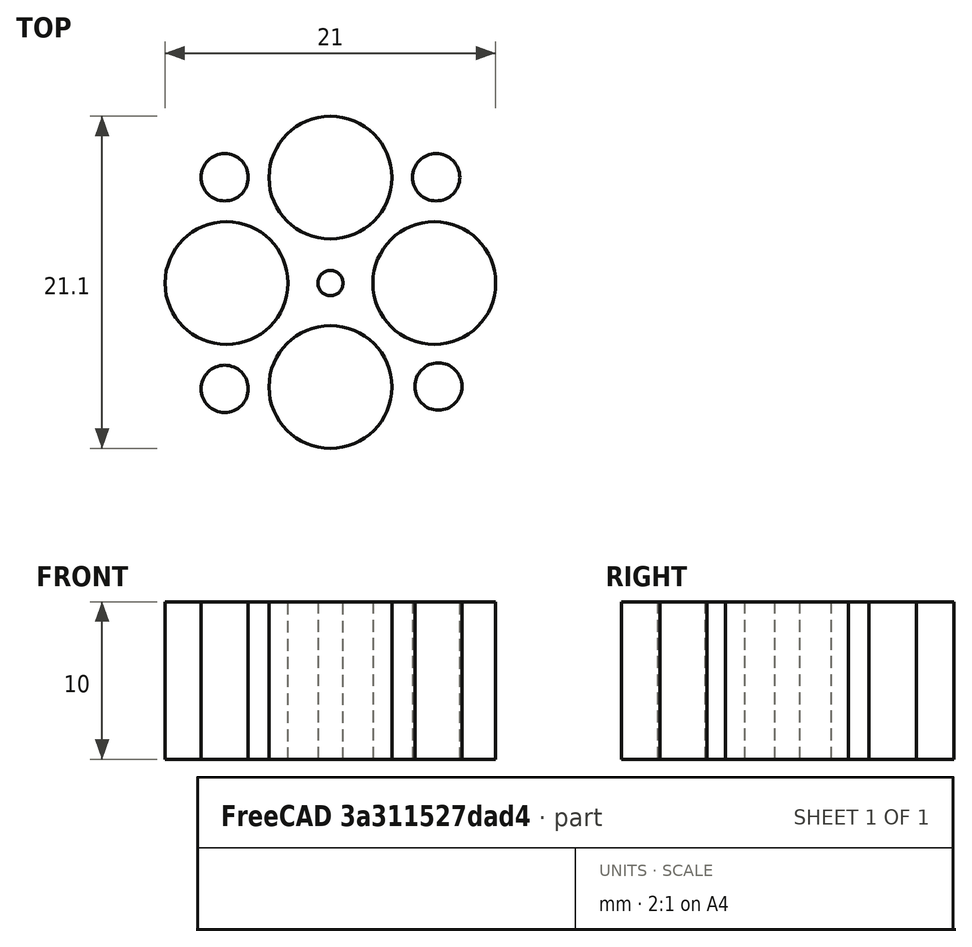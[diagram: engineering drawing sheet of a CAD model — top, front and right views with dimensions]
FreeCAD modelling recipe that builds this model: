
FCSTD DOCUMENT  (FreeCAD 0.19R0.19.2)
Label: 007
License: All rights reserved
LicenseURL: http://en.wikipedia.org/wiki/All_rights_reserved
objects: Sketcher::SketchObject×2, Part::Extrusion×1
note: 3 computed .brp shape members not serialized (recipe doc carries the construction recipe); baked Part::Feature solids carry a one-line shape summary decoded from their .brp

FEATURE [Sketcher::SketchObject] Sketch  label="holes"
  FullyConstrained = true
  sketch-geometry (9):
    g0: Circle CenterX=0 CenterY=0 CenterZ=0 NormalX=0 NormalY=0 NormalZ=1 AngleXU=0 Radius=0.8
    g1: Circle CenterX=0 CenterY=6.7 CenterZ=0 NormalX=0 NormalY=0 NormalZ=1 AngleXU=0 Radius=3.9
    g2: Circle CenterX=6.6 CenterY=0 CenterZ=0 NormalX=0 NormalY=0 NormalZ=1 AngleXU=0 Radius=3.9
    g3: Circle CenterX=-6.6 CenterY=0 CenterZ=0 NormalX=0 NormalY=0 NormalZ=1 AngleXU=0 Radius=3.9
    g4: Circle CenterX=0 CenterY=-6.6 CenterZ=0 NormalX=0 NormalY=0 NormalZ=1 AngleXU=0 Radius=3.9
    g5: Circle CenterX=6.71751 CenterY=6.71751 CenterZ=0 NormalX=0 NormalY=0 NormalZ=1 AngleXU=0 Radius=1.5
    g6: Circle CenterX=-6.71751 CenterY=-6.71751 CenterZ=0 NormalX=0 NormalY=0 NormalZ=1 AngleXU=0 Radius=1.5
    g7: Circle CenterX=-6.71751 CenterY=6.71751 CenterZ=0 NormalX=0 NormalY=0 NormalZ=1 AngleXU=0 Radius=1.5
    g8: Circle CenterX=6.86196 CenterY=-6.56989 CenterZ=0 NormalX=0 NormalY=0 NormalZ=1 AngleXU=0 Radius=1.5
  constraints (9):
    c: Block(g5)
    c: Block(g2)
    c: Block(g1)
    c: Block(g7)
    c: Block(g3)
    c: Block(g6)
    c: Block(g4)
    c: Block(g0)
    c: Block(g8)
FEATURE [Part::Extrusion] Extrude
  Base = -> Sketch
  Dir = (0,0,1)
  DirMode = 2
  FaceMakerClass = Part::FaceMakerBullseye
  LengthFwd = 10
  LengthRev = 0
  Solid = true
  Symmetric = false
FEATURE [Sketcher::SketchObject] Sketch001
  FullyConstrained = true
  Placement = pos=(0,0,0) rot=(0.57735,0.57735,0.57735;2.0944rad)
  sketch-geometry (25):
    g0: LineSegment StartX=1.6 StartY=4 StartZ=0 EndX=0 EndY=4 EndZ=0
    g1: Circle CenterX=12.5 CenterY=0.7 CenterZ=0 NormalX=0 NormalY=0 NormalZ=1 AngleXU=0 Radius=1
    g2: Circle CenterX=13.06 CenterY=0 CenterZ=0 NormalX=0 NormalY=0 NormalZ=1 AngleXU=0 Radius=1
    g3: Circle CenterX=12.5 CenterY=-0.7 CenterZ=0 NormalX=0 NormalY=0 NormalZ=1 AngleXU=0 Radius=1
    g4: BSplineCurve PolesCount=3 KnotsCount=2 Degree=2 IsPeriodic=0
    g5: GeomPoint X=12.5 Y=0.7 Z=0
    g6: GeomPoint X=12.5 Y=-0.7 Z=0
    g7: LineSegment StartX=12.5 StartY=0.7 StartZ=0 EndX=3.81896 EndY=1.5 EndZ=0
    g8: LineSegment StartX=12.5 StartY=-0.7 StartZ=0 EndX=3.81896 EndY=-1.5 EndZ=0
    g9: LineSegment StartX=3.81896 StartY=1.5 StartZ=0 EndX=2.61896 EndY=1.5 EndZ=0
    g10: Circle CenterX=1.6 CenterY=4 CenterZ=0 NormalX=0 NormalY=0 NormalZ=1 AngleXU=0 Radius=1
    g11: Circle CenterX=1.96118 CenterY=1.73941 CenterZ=0 NormalX=0 NormalY=0 NormalZ=1 AngleXU=0 Radius=1
    g12: Circle CenterX=2.61896 CenterY=1.5 CenterZ=0 NormalX=0 NormalY=0 NormalZ=1 AngleXU=0 Radius=1
    g13: BSplineCurve PolesCount=3 KnotsCount=2 Degree=2 IsPeriodic=0
    g14: GeomPoint X=1.6 Y=4 Z=0
    g15: GeomPoint X=2.61896 Y=1.5 Z=0
    g16: LineSegment StartX=1.6 StartY=-4 StartZ=0 EndX=0 EndY=-4 EndZ=0
    g17: LineSegment StartX=0 StartY=-4 StartZ=0 EndX=0 EndY=4 EndZ=0
    g18: LineSegment StartX=3.81896 StartY=-1.5 StartZ=0 EndX=2.61896 EndY=-1.5 EndZ=0
    g19: Circle CenterX=1.6 CenterY=-4 CenterZ=0 NormalX=0 NormalY=0 NormalZ=1 AngleXU=0 Radius=1
    g20: Circle CenterX=1.96118 CenterY=-1.73941 CenterZ=0 NormalX=0 NormalY=0 NormalZ=1 AngleXU=0 Radius=1
    g21: Circle CenterX=2.61896 CenterY=-1.5 CenterZ=0 NormalX=0 NormalY=0 NormalZ=1 AngleXU=0 Radius=1
    g22: BSplineCurve PolesCount=3 KnotsCount=2 Degree=2 IsPeriodic=0
    g23: GeomPoint X=1.6 Y=-4 Z=0
    g24: GeomPoint X=2.61896 Y=-1.5 Z=0
  constraints (51):
    c: Horizontal(g0)
    c: Distance(g0) = 1.6
    c: Weight(g1) = 1
    c: Equal(g1,g2)
    c: Equal(g1,g3)
    c: InternalAlignment(g1,g4)
    c: InternalAlignment(g2,g4)
    c: InternalAlignment(g3,g4)
    c: InternalAlignment(g5,g4)
    c: InternalAlignment(g6,g4)
    c: Block(g4)
    c: Block(g0)
    c: Coincident(g7,g4)
    c: Coincident(g8,g4)
    c: Horizontal(g9)
    c: Distance(g9) = 1.2
    c: Coincident(g13,g0)
    c: Weight(g10) = 1
    c: Equal(g10,g11)
    c: Equal(g10,g12)
    c: Coincident(g13,g9)
    c: InternalAlignment(g10,g13)
    c: InternalAlignment(g11,g13)
    c: InternalAlignment(g12,g13)
    c: InternalAlignment(g14,g13)
    c: InternalAlignment(g15,g13)
    c: Block(g9)
    c: Block(g7)
    c: Horizontal(g16)
    c: Distance(g16) = 1.6
    c: Coincident(g17,g16)
    c: Coincident(g17,g0)
    c: Vertical(g17)
    c: Block(g8)
    c: Block(g16)
    c: Horizontal(g18)
    c: Equal(g9,g18) = 1.2
    c: Block(g18)
    c: Coincident(g18,g8)
    c: Coincident(g22,g16)
    c: Weight(g19) = 1
    c: Equal(g19,g20)
    c: Equal(g19,g21)
    c: Coincident(g22,g18)
    c: InternalAlignment(g19,g22)
    c: InternalAlignment(g20,g22)
    c: InternalAlignment(g21,g22)
    c: InternalAlignment(g23,g22)
    c: InternalAlignment(g24,g22)
    c: Block(g22)
    c: Block(g13)
